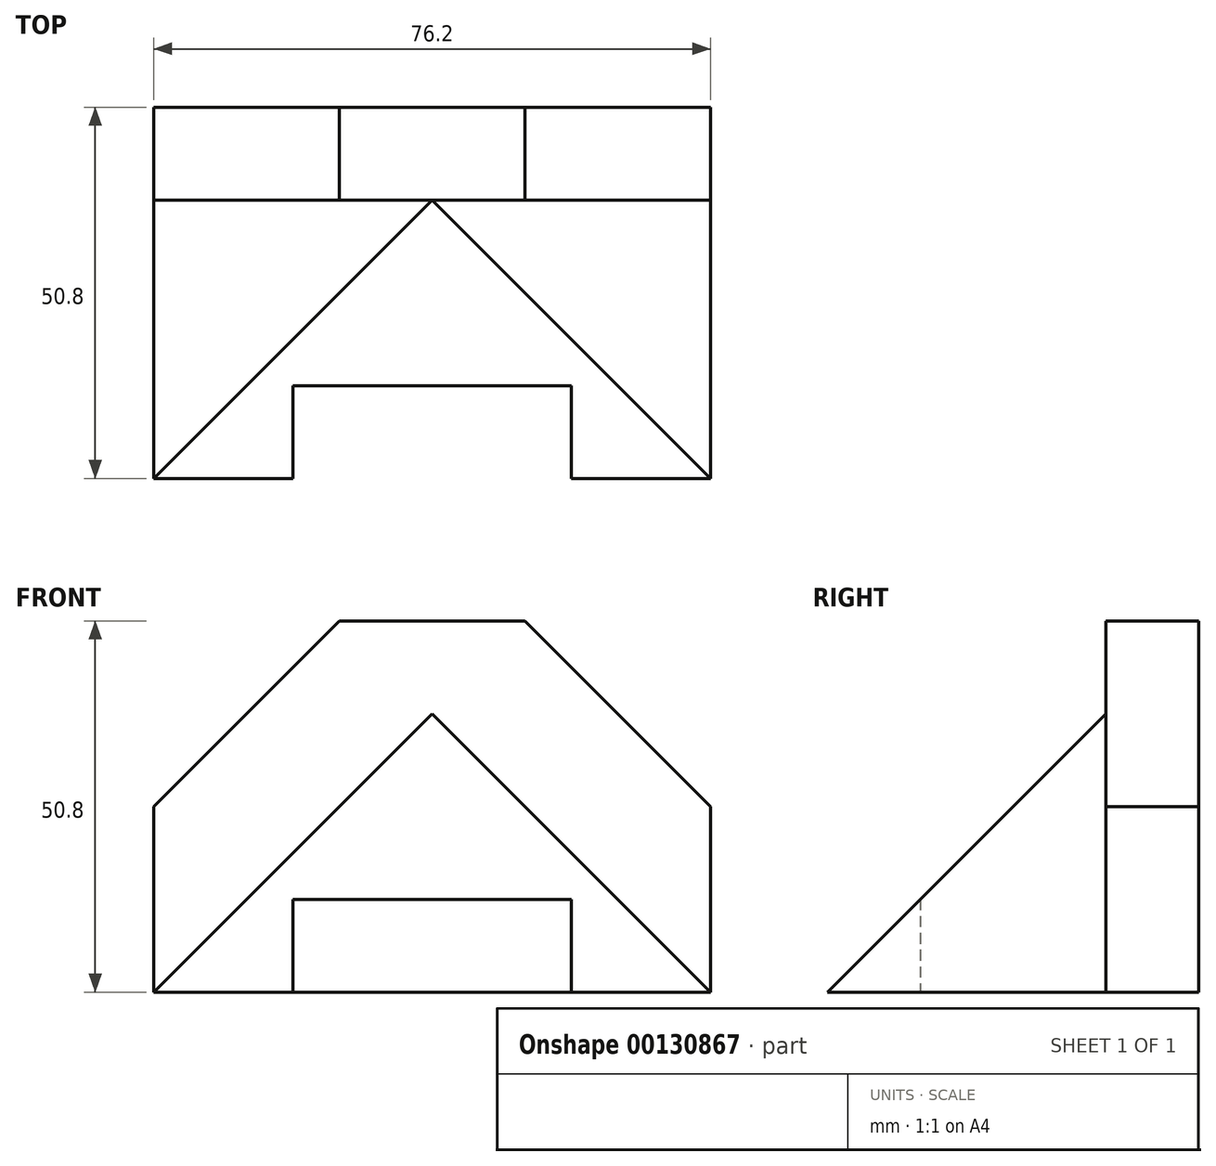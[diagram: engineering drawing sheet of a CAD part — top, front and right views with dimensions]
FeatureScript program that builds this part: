
annotation { "Feature Type Name" : "Feature", "Feature Type Description" : "" }
export const myFeature = defineFeature(function(context is Context, id is Id, definition is map)
    precondition{}
    {
        {
            var Q0;
            Q0=qCreatedBy(makeId("Front.planeOp"),FACE);
            var sketch = newSketch(context, id + "F0", { "sketchPlane" : qUnion([Q0])});
            skLineSegment(sketch, "E0", {"start": v(0, 0) * mm, "end": v(0, 25.4) * mm});
            skLineSegment(sketch, "E1", {"start": v(0, 0) * mm, "end": v(76.2, 0) * mm});
            skLineSegment(sketch, "E2", {"start": v(76.2, 0) * mm, "end": v(76.2, 25.4) * mm});
            skLineSegment(sketch, "E3", {"start": v(0, 0) * mm, "end": v(25.4, 0) * mm, "construction": true});
            skLineSegment(sketch, "E4", {"start": v(25.4, 0) * mm, "end": v(25.4, 50.8) * mm, "construction": true});
            skLineSegment(sketch, "E5", {"start": v(0, 25.4) * mm, "end": v(25.4, 50.8) * mm});
            skLineSegment(sketch, "E6", {"start": v(25.4, 50.8) * mm, "end": v(50.8, 50.8) * mm});
            skLineSegment(sketch, "E7", {"start": v(50.8, 50.8) * mm, "end": v(76.2, 25.4) * mm});
            skSolve(sketch);
        }
        {
            var Q0;
            Q0=makeQuery(id+"F0.imprint","IMPRINT",FACE,{"disambiguationData":[TD([[makeQuery(id+"F0.imprint","IMPRINT",EDGE,{"derivedFrom":sQuery(id+"F0.wireOp",EDGE,"E0")}),-1.0]])]});
            extrude(context, id + "F1", {"entities" : qUnion([Q0]), "depth" : 12.7 * mm});
        }
        {
            var Q0;
            Q0=makeQuery(id+"F1.opExtrude","CAP_FACE",FACE,{"disambiguationData":[OSD([sQuery(id+"F0.wireOp",EDGE,"E0"),sQuery(id+"F0.wireOp",EDGE,"E1"),sQuery(id+"F0.wireOp",EDGE,"E2"),sQuery(id+"F0.wireOp",EDGE,"E5"),sQuery(id+"F0.wireOp",EDGE,"E6"),sQuery(id+"F0.wireOp",EDGE,"E7")])],"isStart":false});
            var sketch = newSketch(context, id + "F2", { "sketchPlane" : qUnion([Q0])});
            skLineSegment(sketch, "E8", {"start": v(38.1, 0) * mm, "end": v(38.1, 38.1) * mm, "construction": true});
            skLineSegment(sketch, "E9", {"start": v(0, 0) * mm, "end": v(76.2, 0) * mm});
            skLineSegment(sketch, "E10", {"start": v(76.2, 0) * mm, "end": v(38.1, 38.1) * mm});
            skLineSegment(sketch, "E11", {"start": v(38.1, 38.1) * mm, "end": v(0, 0) * mm});
            skSolve(sketch);
        }
        {
            var Q0;
            Q0=makeQuery(id+"F2.imprint","IMPRINT",FACE,{"disambiguationData":[TD([[makeQuery(id+"F2.imprint","IMPRINT",EDGE,{"derivedFrom":sQuery(id+"F2.wireOp",EDGE,"E9")}),1.0]])]});
            extrude(context, id + "F3", {"entities" : qUnion([Q0]), "operationType" : NewBodyOperationType.ADD, "depth" : 38.1 * mm});
        }
        {
            var Q0;
            Q0=makeQuery(id+"F1.opExtrude","SWEPT_FACE",FACE,{"disambiguationData":[OSD([sQuery(id+"F0.wireOp",EDGE,"E2")])]});
            var sketch = newSketch(context, id + "F4", { "sketchPlane" : qUnion([Q0])});
            skLineSegment(sketch, "E12", {"start": v(-12.7, 0) * mm, "end": v(-12.7, 38.1) * mm, "construction": true});
            skLineSegment(sketch, "E13", {"start": v(-12.7, 0) * mm, "end": v(-50.8, 0) * mm, "construction": true});
            skLineSegment(sketch, "E14", {"start": v(-50.8, 0) * mm, "end": v(-12.7, 38.1) * mm});
            skLineSegment(sketch, "E15", {"start": v(-12.7, 38.1) * mm, "end": v(-50.8, 38.1) * mm});
            skLineSegment(sketch, "E16", {"start": v(-50.8, 38.1) * mm, "end": v(-50.8, 0) * mm});
            skSolve(sketch);
        }
        {
            var Q0;
            Q0=makeQuery(id+"F4.imprint","IMPRINT",FACE,{"disambiguationData":[TD([[makeQuery(id+"F4.imprint","IMPRINT",EDGE,{"derivedFrom":sQuery(id+"F4.wireOp",EDGE,"E14")}),1.0]])]});
            extrude(context, id + "F5", {"entities" : qUnion([Q0]), "operationType" : NewBodyOperationType.REMOVE, "oppositeDirection" : true, "depth" : 76.2 * mm});
        }
        {
            var Q0;
            Q0=qCreatedBy(makeId("Top.planeOp"),FACE);
            var sketch = newSketch(context, id + "F6", { "sketchPlane" : qUnion([Q0])});
            skLineSegment(sketch, "E17", {"start": v(0, 0) * mm, "end": v(0, -50.8) * mm, "construction": true});
            skLineSegment(sketch, "E18", {"start": v(0, -50.8) * mm, "end": v(19.05, -50.8) * mm, "construction": true});
            skLineSegment(sketch, "E19", {"start": v(19.05, -50.8) * mm, "end": v(19.05, -38.1) * mm});
            skLineSegment(sketch, "E20", {"start": v(19.05, -38.1) * mm, "end": v(57.15, -38.1) * mm});
            skLineSegment(sketch, "E21", {"start": v(57.15, -38.1) * mm, "end": v(57.15, -50.8) * mm});
            skLineSegment(sketch, "E22", {"start": v(57.15, -50.8) * mm, "end": v(19.05, -50.8) * mm});
            skSolve(sketch);
        }
        {
            var Q0;
            Q0=makeQuery(id+"F6.imprint","IMPRINT",FACE,{"disambiguationData":[TD([[makeQuery(id+"F6.imprint","IMPRINT",EDGE,{"derivedFrom":sQuery(id+"F6.wireOp",EDGE,"E19")}),-1.0]])]});
            extrude(context, id + "F7", {"entities" : qUnion([Q0]), "operationType" : NewBodyOperationType.REMOVE, "depth" : 25.4 * mm});
        }
    });
